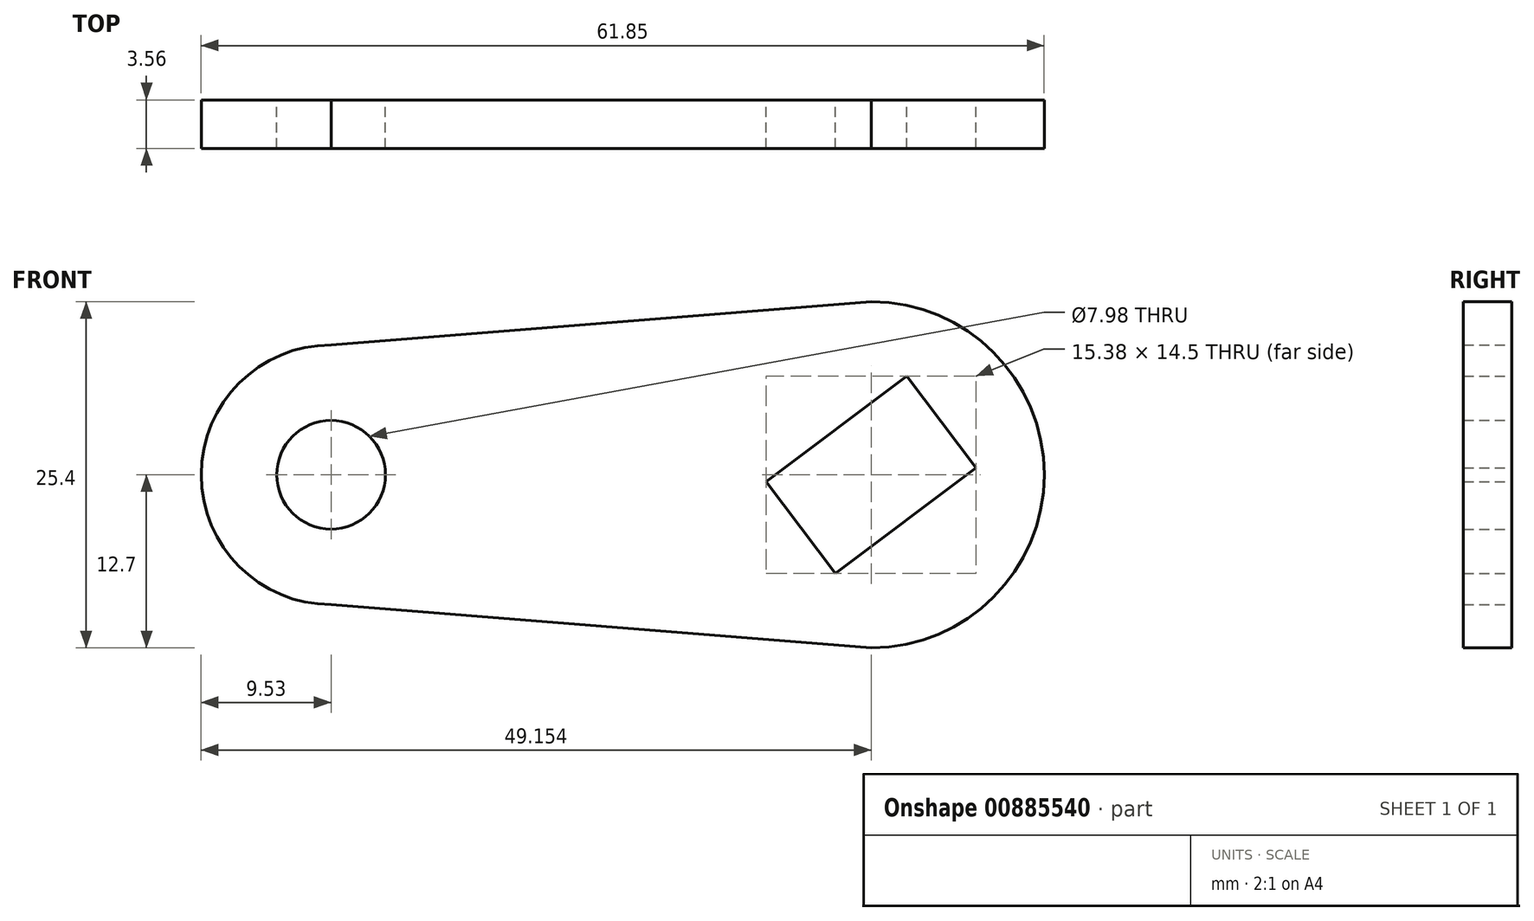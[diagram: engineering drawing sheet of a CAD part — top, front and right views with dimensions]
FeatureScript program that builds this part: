
annotation { "Feature Type Name" : "Feature", "Feature Type Description" : "" }
export const myFeature = defineFeature(function(context is Context, id is Id, definition is map)
    precondition{}
    {
        {
            var Q0;
            Q0=qCreatedBy(makeId("Front.planeOp"),FACE);
            var sketch = newSketch(context, id + "F0", { "sketchPlane" : qUnion([Q0])});
            skCircle(sketch, "E0", {"center": v(0, 0) * mm, "radius": 3.99 * mm});
            skArc(sketch, "E1", {"start": v(0, 9.53) * mm, "mid": v(-9.53, 0) * mm, "end": v(0, -9.53) * mm});
            skPoint(sketch, "E2.middle", {"position": v(39.62, 0) * mm});
            skLineSegment(sketch, "E3", {"start": v(31.93, -0.52) * mm, "end": v(42.24, 7.25) * mm});
            skLineSegment(sketch, "E4", {"start": v(42.24, 7.25) * mm, "end": v(47.31, 0.52) * mm});
            skLineSegment(sketch, "E5", {"start": v(47.31, 0.52) * mm, "end": v(37, -7.25) * mm});
            skLineSegment(sketch, "E6", {"start": v(37, -7.25) * mm, "end": v(31.93, -0.52) * mm});
            skLineSegment(sketch, "E7", {"start": v(39.62, 0) * mm, "end": v(70.61, 23.35) * mm, "construction": true});
            skLineSegment(sketch, "E8", {"start": v(39.62, 0) * mm, "end": v(57.6, -23.85) * mm, "construction": true});
            skLineSegment(sketch, "E9", {"start": v(39.62, 0) * mm, "end": v(39.62, 30.68) * mm, "construction": true});
            skLineSegment(sketch, "E10", {"start": v(39.62, 0) * mm, "end": v(39.62, -19.08) * mm, "construction": true});
            skArc(sketch, "E11", {"start": v(39.62, -12.7) * mm, "mid": v(52.32, 0) * mm, "end": v(39.62, 12.7) * mm});
            skLineSegment(sketch, "E12", {"start": v(0, 9.53) * mm, "end": v(39.62, 12.7) * mm});
            skLineSegment(sketch, "E13", {"start": v(0, -9.53) * mm, "end": v(39.62, -12.7) * mm});
            skSolve(sketch);
        }
        {
            var Q0;
            Q0=makeQuery(id+"F0.imprint","IMPRINT",FACE,{"disambiguationData":[TD([[makeQuery(id+"F0.imprint","IMPRINT",EDGE,{"derivedFrom":sQuery(id+"F0.wireOp",EDGE,"E0")}),-1.0]])]});
            extrude(context, id + "F1", {"entities" : qUnion([Q0]), "depth" : 3.56 * mm, "offsetDistance" : 25.4 * mm});
        }
    });
